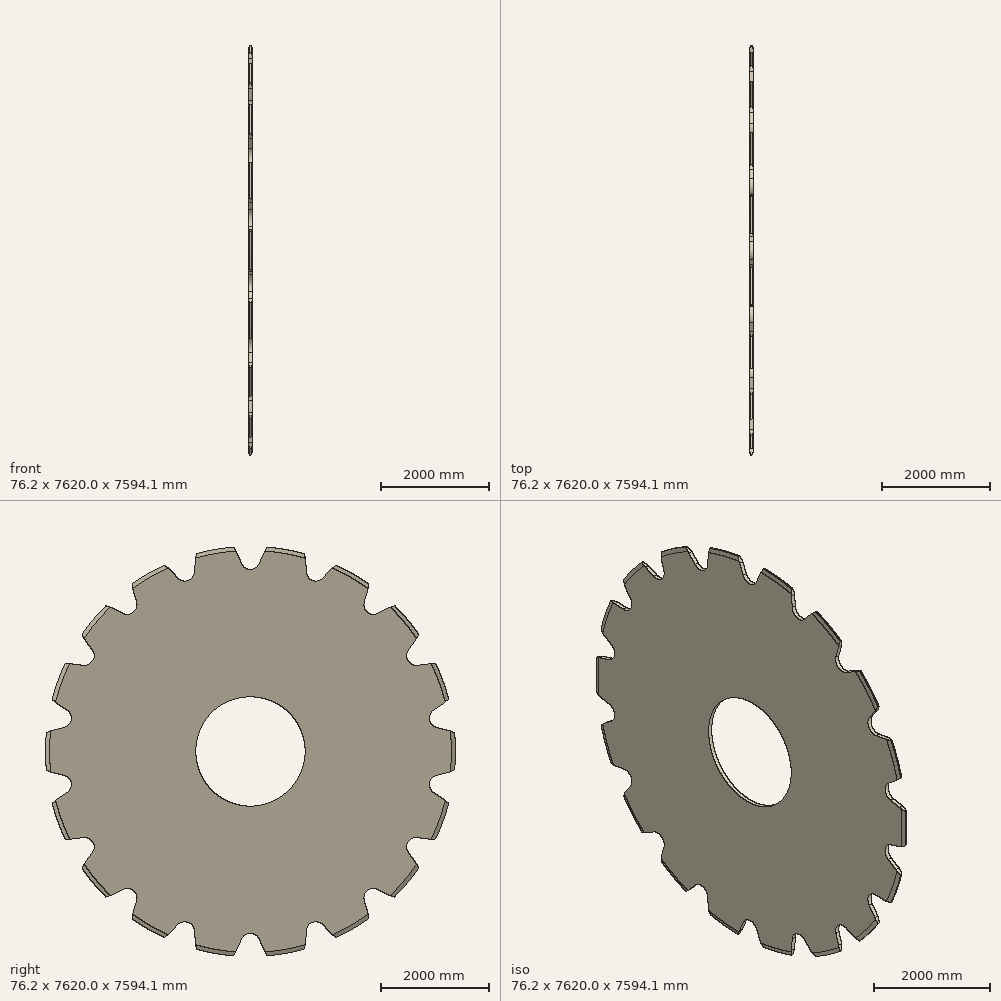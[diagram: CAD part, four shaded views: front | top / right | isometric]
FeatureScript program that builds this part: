
annotation { "Feature Type Name" : "Feature", "Feature Type Description" : "" }
export const myFeature = defineFeature(function(context is Context, id is Id, definition is map)
    precondition{}
    {
        {
            var Q0;
            Q0=qCreatedBy(makeId("Front.planeOp"),FACE);
            var sketch = newSketch(context, id + "F0", { "sketchPlane" : qUnion([Q0])});
            skLineSegment(sketch, "E0", {"start": v(0, 0) * mm, "end": v(-519.36, 0) * mm, "construction": true});
            skLineSegment(sketch, "E1", {"start": v(-38.1, 1016) * mm, "end": v(-38.1, 3733.8) * mm});
            skLineSegment(sketch, "E2", {"start": v(-38.1, 3733.8) * mm, "end": v(-12.7, 3810) * mm});
            skLineSegment(sketch, "E3", {"start": v(-12.7, 3810) * mm, "end": v(12.7, 3810) * mm});
            skLineSegment(sketch, "E4", {"start": v(12.7, 3810) * mm, "end": v(38.1, 3733.8) * mm});
            skLineSegment(sketch, "E5", {"start": v(38.1, 3733.8) * mm, "end": v(38.1, 1016) * mm});
            skLineSegment(sketch, "E6", {"start": v(38.1, 1016) * mm, "end": v(-38.1, 1016) * mm});
            skLineSegment(sketch, "E7", {"start": v(0, 0) * mm, "end": v(0, -208.55) * mm, "construction": true});
            skSolve(sketch);
        }
        {
            var Q0;
            Q0 = qSketchRegion(id + "F0", true);
            var Q1;
            Q1=sQuery(id+"F0.wireOp",EDGE,"E0");
            revolve(context, id + "F1", {"surfaceOperationType" : NewSurfaceOperationType.NEW, "entities" : qUnion([Q0]), "axis" : qUnion([Q1]), "revolveType" : RevolveType.FULL});
        }
        {
            var Q0;
            Q0=makeQuery(id+"F1.opRevolve","SWEPT_FACE",FACE,{"disambiguationData":[OSD([sQuery(id+"F0.wireOp",EDGE,"E5")])]});
            var sketch = newSketch(context, id + "F2", { "sketchPlane" : qUnion([Q0])});
            skLineSegment(sketch, "E8", {"start": v(0, 0) * mm, "end": v(0, -5755.4) * mm, "construction": true});
            skArc(sketch, "E9", {"start": v(162.88, -3484.7) * mm, "mid": v(0, -3378.2) * mm, "end": v(-162.88, -3484.7) * mm});
            skLineSegment(sketch, "E10", {"start": v(162.88, -3484.7) * mm, "end": v(254, -3692.86) * mm});
            skLineSegment(sketch, "E11", {"start": v(254, -3692.86) * mm, "end": v(381, -3912.83) * mm});
            skLineSegment(sketch, "E12.MirrorCS", {"start": v(-162.88, -3484.7) * mm, "end": v(-254, -3692.86) * mm});
            skLineSegment(sketch, "E13.MirrorCS", {"start": v(-254, -3692.86) * mm, "end": v(-381, -3912.83) * mm});
            skLineSegment(sketch, "E14", {"start": v(381, -3912.83) * mm, "end": v(-381, -3912.83) * mm});
            skLineSegment(sketch, "E15.1.0", {"start": v(1696.29, -3546.55) * mm, "end": v(980.24, -3807.17) * mm});
            skLineSegment(sketch, "E15.1.1", {"start": v(1501.71, -3383.28) * mm, "end": v(1696.29, -3546.55) * mm});
            skLineSegment(sketch, "E15.1.2", {"start": v(1344.9, -3218.84) * mm, "end": v(1501.71, -3383.28) * mm});
            skArc(sketch, "E15.1.3", {"start": v(1344.9, -3218.84) * mm, "mid": v(1155.41, -3174.47) * mm, "end": v(1038.78, -3330.25) * mm});
            skLineSegment(sketch, "E15.1.4", {"start": v(1038.78, -3330.25) * mm, "end": v(1024.35, -3557.02) * mm});
            skLineSegment(sketch, "E15.1.5", {"start": v(1024.35, -3557.02) * mm, "end": v(980.24, -3807.17) * mm});
            skLineSegment(sketch, "E15.2.0", {"start": v(2806.98, -2752.5) * mm, "end": v(2223.25, -3242.3) * mm});
            skLineSegment(sketch, "E15.2.1", {"start": v(2568.3, -2665.62) * mm, "end": v(2806.98, -2752.5) * mm});
            skLineSegment(sketch, "E15.2.2", {"start": v(2364.7, -2564.74) * mm, "end": v(2568.3, -2665.62) * mm});
            skArc(sketch, "E15.2.3", {"start": v(2364.7, -2564.74) * mm, "mid": v(2171.47, -2587.85) * mm, "end": v(2115.15, -2774.13) * mm});
            skLineSegment(sketch, "E15.2.4", {"start": v(2115.15, -2774.13) * mm, "end": v(2179.15, -2992.16) * mm});
            skLineSegment(sketch, "E15.2.5", {"start": v(2179.15, -2992.16) * mm, "end": v(2223.25, -3242.3) * mm});
            skLineSegment(sketch, "E15.3.0", {"start": v(3579.1, -1626.46) * mm, "end": v(3198.1, -2286.37) * mm});
            skLineSegment(sketch, "E15.3.1", {"start": v(3325.1, -1626.46) * mm, "end": v(3579.1, -1626.46) * mm});
            skLineSegment(sketch, "E15.3.2", {"start": v(3099.28, -1601.3) * mm, "end": v(3325.1, -1626.46) * mm});
            skArc(sketch, "E15.3.3", {"start": v(3099.28, -1601.3) * mm, "mid": v(2925.6, -1689.1) * mm, "end": v(2936.4, -1883.4) * mm});
            skLineSegment(sketch, "E15.3.4", {"start": v(2936.4, -1883.4) * mm, "end": v(3071.1, -2066.4) * mm});
            skLineSegment(sketch, "E15.3.5", {"start": v(3071.1, -2066.4) * mm, "end": v(3198.1, -2286.37) * mm});
            skLineSegment(sketch, "E15.4.0", {"start": v(3919.54, -304.24) * mm, "end": v(3787.22, -1054.67) * mm});
            skLineSegment(sketch, "E15.4.1", {"start": v(3680.86, -391.12) * mm, "end": v(3919.54, -304.24) * mm});
            skLineSegment(sketch, "E15.4.2", {"start": v(3460.04, -444.7) * mm, "end": v(3680.86, -391.12) * mm});
            skArc(sketch, "E15.4.3", {"start": v(3460.04, -444.7) * mm, "mid": v(3326.88, -586.62) * mm, "end": v(3403.48, -765.51) * mm});
            skLineSegment(sketch, "E15.4.4", {"start": v(3403.48, -765.51) * mm, "end": v(3592.65, -891.4) * mm});
            skLineSegment(sketch, "E15.4.5", {"start": v(3592.65, -891.4) * mm, "end": v(3787.22, -1054.67) * mm});
            skLineSegment(sketch, "E15.5.0", {"start": v(3787.22, 1054.67) * mm, "end": v(3919.54, 304.24) * mm});
            skLineSegment(sketch, "E15.5.1", {"start": v(3592.65, 891.4) * mm, "end": v(3787.22, 1054.67) * mm});
            skLineSegment(sketch, "E15.5.2", {"start": v(3403.48, 765.51) * mm, "end": v(3592.65, 891.4) * mm});
            skArc(sketch, "E15.5.3", {"start": v(3403.48, 765.51) * mm, "mid": v(3326.88, 586.62) * mm, "end": v(3460.04, 444.7) * mm});
            skLineSegment(sketch, "E15.5.4", {"start": v(3460.04, 444.7) * mm, "end": v(3680.86, 391.12) * mm});
            skLineSegment(sketch, "E15.5.5", {"start": v(3680.86, 391.12) * mm, "end": v(3919.54, 304.24) * mm});
            skPoint(sketch, "E15.center", {"position": v(0, 0) * mm});
            skLineSegment(sketch, "E16.2.6.0", {"start": v(3198.1, 2286.37) * mm, "end": v(3579.1, 1626.46) * mm});
            skLineSegment(sketch, "E16.3.6.0", {"start": v(3071.1, 2066.4) * mm, "end": v(3198.1, 2286.37) * mm});
            skLineSegment(sketch, "E16.6.6.0", {"start": v(2936.4, 1883.4) * mm, "end": v(3071.1, 2066.4) * mm});
            skArc(sketch, "E16.9.6.0", {"start": v(2936.4, 1883.4) * mm, "mid": v(2925.6, 1689.1) * mm, "end": v(3099.28, 1601.3) * mm});
            skLineSegment(sketch, "E16.13.6.0", {"start": v(3099.28, 1601.3) * mm, "end": v(3325.1, 1626.46) * mm});
            skLineSegment(sketch, "E16.16.6.0", {"start": v(3325.1, 1626.46) * mm, "end": v(3579.1, 1626.46) * mm});
            skLineSegment(sketch, "E16.2.7.0", {"start": v(2223.25, 3242.3) * mm, "end": v(2806.98, 2752.5) * mm});
            skLineSegment(sketch, "E16.3.7.0", {"start": v(2179.15, 2992.16) * mm, "end": v(2223.25, 3242.3) * mm});
            skLineSegment(sketch, "E16.6.7.0", {"start": v(2115.15, 2774.13) * mm, "end": v(2179.15, 2992.16) * mm});
            skArc(sketch, "E16.9.7.0", {"start": v(2115.15, 2774.13) * mm, "mid": v(2171.47, 2587.85) * mm, "end": v(2364.7, 2564.74) * mm});
            skLineSegment(sketch, "E16.13.7.0", {"start": v(2364.7, 2564.74) * mm, "end": v(2568.3, 2665.62) * mm});
            skLineSegment(sketch, "E16.16.7.0", {"start": v(2568.3, 2665.62) * mm, "end": v(2806.98, 2752.5) * mm});
            skLineSegment(sketch, "E16.2.8.0", {"start": v(980.24, 3807.17) * mm, "end": v(1696.29, 3546.55) * mm});
            skLineSegment(sketch, "E16.3.8.0", {"start": v(1024.35, 3557.02) * mm, "end": v(980.24, 3807.17) * mm});
            skLineSegment(sketch, "E16.6.8.0", {"start": v(1038.78, 3330.25) * mm, "end": v(1024.35, 3557.02) * mm});
            skArc(sketch, "E16.9.8.0", {"start": v(1038.78, 3330.25) * mm, "mid": v(1155.41, 3174.47) * mm, "end": v(1344.9, 3218.84) * mm});
            skLineSegment(sketch, "E16.13.8.0", {"start": v(1344.9, 3218.84) * mm, "end": v(1501.71, 3383.28) * mm});
            skLineSegment(sketch, "E16.16.8.0", {"start": v(1501.71, 3383.28) * mm, "end": v(1696.29, 3546.55) * mm});
            skLineSegment(sketch, "E16.2.9.0", {"start": v(-381, 3912.83) * mm, "end": v(381, 3912.83) * mm});
            skLineSegment(sketch, "E16.3.9.0", {"start": v(-254, 3692.86) * mm, "end": v(-381, 3912.83) * mm});
            skLineSegment(sketch, "E16.6.9.0", {"start": v(-162.88, 3484.7) * mm, "end": v(-254, 3692.86) * mm});
            skArc(sketch, "E16.9.9.0", {"start": v(-162.88, 3484.7) * mm, "mid": v(0, 3378.2) * mm, "end": v(162.88, 3484.7) * mm});
            skLineSegment(sketch, "E16.13.9.0", {"start": v(162.88, 3484.7) * mm, "end": v(254, 3692.86) * mm});
            skLineSegment(sketch, "E16.16.9.0", {"start": v(254, 3692.86) * mm, "end": v(381, 3912.83) * mm});
            skLineSegment(sketch, "E16.2.10.0", {"start": v(-1696.29, 3546.55) * mm, "end": v(-980.24, 3807.17) * mm});
            skLineSegment(sketch, "E16.3.10.0", {"start": v(-1501.71, 3383.28) * mm, "end": v(-1696.29, 3546.55) * mm});
            skLineSegment(sketch, "E16.6.10.0", {"start": v(-1344.9, 3218.84) * mm, "end": v(-1501.71, 3383.28) * mm});
            skArc(sketch, "E16.9.10.0", {"start": v(-1344.9, 3218.84) * mm, "mid": v(-1155.41, 3174.47) * mm, "end": v(-1038.78, 3330.25) * mm});
            skLineSegment(sketch, "E16.13.10.0", {"start": v(-1038.78, 3330.25) * mm, "end": v(-1024.35, 3557.02) * mm});
            skLineSegment(sketch, "E16.16.10.0", {"start": v(-1024.35, 3557.02) * mm, "end": v(-980.24, 3807.17) * mm});
            skLineSegment(sketch, "E16.2.11.0", {"start": v(-2806.98, 2752.5) * mm, "end": v(-2223.25, 3242.3) * mm});
            skLineSegment(sketch, "E16.3.11.0", {"start": v(-2568.3, 2665.62) * mm, "end": v(-2806.98, 2752.5) * mm});
            skLineSegment(sketch, "E16.6.11.0", {"start": v(-2364.7, 2564.74) * mm, "end": v(-2568.3, 2665.62) * mm});
            skArc(sketch, "E16.9.11.0", {"start": v(-2364.7, 2564.74) * mm, "mid": v(-2171.47, 2587.85) * mm, "end": v(-2115.15, 2774.13) * mm});
            skLineSegment(sketch, "E16.13.11.0", {"start": v(-2115.15, 2774.13) * mm, "end": v(-2179.15, 2992.16) * mm});
            skLineSegment(sketch, "E16.16.11.0", {"start": v(-2179.15, 2992.16) * mm, "end": v(-2223.25, 3242.3) * mm});
            skLineSegment(sketch, "E16.2.12.0", {"start": v(-3579.1, 1626.46) * mm, "end": v(-3198.1, 2286.37) * mm});
            skLineSegment(sketch, "E16.3.12.0", {"start": v(-3325.1, 1626.46) * mm, "end": v(-3579.1, 1626.46) * mm});
            skLineSegment(sketch, "E16.6.12.0", {"start": v(-3099.28, 1601.3) * mm, "end": v(-3325.1, 1626.46) * mm});
            skArc(sketch, "E16.9.12.0", {"start": v(-3099.28, 1601.3) * mm, "mid": v(-2925.6, 1689.1) * mm, "end": v(-2936.4, 1883.4) * mm});
            skLineSegment(sketch, "E16.13.12.0", {"start": v(-2936.4, 1883.4) * mm, "end": v(-3071.1, 2066.4) * mm});
            skLineSegment(sketch, "E16.16.12.0", {"start": v(-3071.1, 2066.4) * mm, "end": v(-3198.1, 2286.37) * mm});
            skLineSegment(sketch, "E16.2.13.0", {"start": v(-3919.54, 304.24) * mm, "end": v(-3787.22, 1054.67) * mm});
            skLineSegment(sketch, "E16.3.13.0", {"start": v(-3680.86, 391.12) * mm, "end": v(-3919.54, 304.24) * mm});
            skLineSegment(sketch, "E16.6.13.0", {"start": v(-3460.04, 444.7) * mm, "end": v(-3680.86, 391.12) * mm});
            skArc(sketch, "E16.9.13.0", {"start": v(-3460.04, 444.7) * mm, "mid": v(-3326.88, 586.62) * mm, "end": v(-3403.48, 765.51) * mm});
            skLineSegment(sketch, "E16.13.13.0", {"start": v(-3403.48, 765.51) * mm, "end": v(-3592.65, 891.4) * mm});
            skLineSegment(sketch, "E16.16.13.0", {"start": v(-3592.65, 891.4) * mm, "end": v(-3787.22, 1054.67) * mm});
            skLineSegment(sketch, "E16.2.14.0", {"start": v(-3787.22, -1054.67) * mm, "end": v(-3919.54, -304.24) * mm});
            skLineSegment(sketch, "E16.3.14.0", {"start": v(-3592.65, -891.4) * mm, "end": v(-3787.22, -1054.67) * mm});
            skLineSegment(sketch, "E16.6.14.0", {"start": v(-3403.48, -765.51) * mm, "end": v(-3592.65, -891.4) * mm});
            skArc(sketch, "E16.9.14.0", {"start": v(-3403.48, -765.51) * mm, "mid": v(-3326.88, -586.62) * mm, "end": v(-3460.04, -444.7) * mm});
            skLineSegment(sketch, "E16.13.14.0", {"start": v(-3460.04, -444.7) * mm, "end": v(-3680.86, -391.12) * mm});
            skLineSegment(sketch, "E16.16.14.0", {"start": v(-3680.86, -391.12) * mm, "end": v(-3919.54, -304.24) * mm});
            skLineSegment(sketch, "E16.2.15.0", {"start": v(-3198.1, -2286.37) * mm, "end": v(-3579.1, -1626.46) * mm});
            skLineSegment(sketch, "E16.3.15.0", {"start": v(-3071.1, -2066.4) * mm, "end": v(-3198.1, -2286.37) * mm});
            skLineSegment(sketch, "E16.6.15.0", {"start": v(-2936.4, -1883.4) * mm, "end": v(-3071.1, -2066.4) * mm});
            skArc(sketch, "E16.9.15.0", {"start": v(-2936.4, -1883.4) * mm, "mid": v(-2925.6, -1689.1) * mm, "end": v(-3099.28, -1601.3) * mm});
            skLineSegment(sketch, "E16.13.15.0", {"start": v(-3099.28, -1601.3) * mm, "end": v(-3325.1, -1626.46) * mm});
            skLineSegment(sketch, "E16.16.15.0", {"start": v(-3325.1, -1626.46) * mm, "end": v(-3579.1, -1626.46) * mm});
            skLineSegment(sketch, "E16.2.16.0", {"start": v(-2223.25, -3242.3) * mm, "end": v(-2806.98, -2752.5) * mm});
            skLineSegment(sketch, "E16.3.16.0", {"start": v(-2179.15, -2992.16) * mm, "end": v(-2223.25, -3242.3) * mm});
            skLineSegment(sketch, "E16.6.16.0", {"start": v(-2115.15, -2774.13) * mm, "end": v(-2179.15, -2992.16) * mm});
            skArc(sketch, "E16.9.16.0", {"start": v(-2115.15, -2774.13) * mm, "mid": v(-2171.47, -2587.85) * mm, "end": v(-2364.7, -2564.74) * mm});
            skLineSegment(sketch, "E16.13.16.0", {"start": v(-2364.7, -2564.74) * mm, "end": v(-2568.3, -2665.62) * mm});
            skLineSegment(sketch, "E16.16.16.0", {"start": v(-2568.3, -2665.62) * mm, "end": v(-2806.98, -2752.5) * mm});
            skLineSegment(sketch, "E16.2.17.0", {"start": v(-980.24, -3807.17) * mm, "end": v(-1696.29, -3546.55) * mm});
            skLineSegment(sketch, "E16.3.17.0", {"start": v(-1024.35, -3557.02) * mm, "end": v(-980.24, -3807.17) * mm});
            skLineSegment(sketch, "E16.6.17.0", {"start": v(-1038.78, -3330.25) * mm, "end": v(-1024.35, -3557.02) * mm});
            skArc(sketch, "E16.9.17.0", {"start": v(-1038.78, -3330.25) * mm, "mid": v(-1155.41, -3174.47) * mm, "end": v(-1344.9, -3218.84) * mm});
            skLineSegment(sketch, "E16.13.17.0", {"start": v(-1344.9, -3218.84) * mm, "end": v(-1501.71, -3383.28) * mm});
            skLineSegment(sketch, "E16.16.17.0", {"start": v(-1501.71, -3383.28) * mm, "end": v(-1696.29, -3546.55) * mm});
            skSolve(sketch);
        }
        {
            var Q0;
            Q0 = qSketchRegion(id + "F2", true);
            extrude(context, id + "F3", {"entities" : qUnion([Q0]), "operationType" : NewBodyOperationType.REMOVE, "endBound" : BoundingType.THROUGH_ALL, "oppositeDirection" : true, "depth" : 25.4 * mm, "offsetDistance" : 25.4 * mm});
        }
    });
